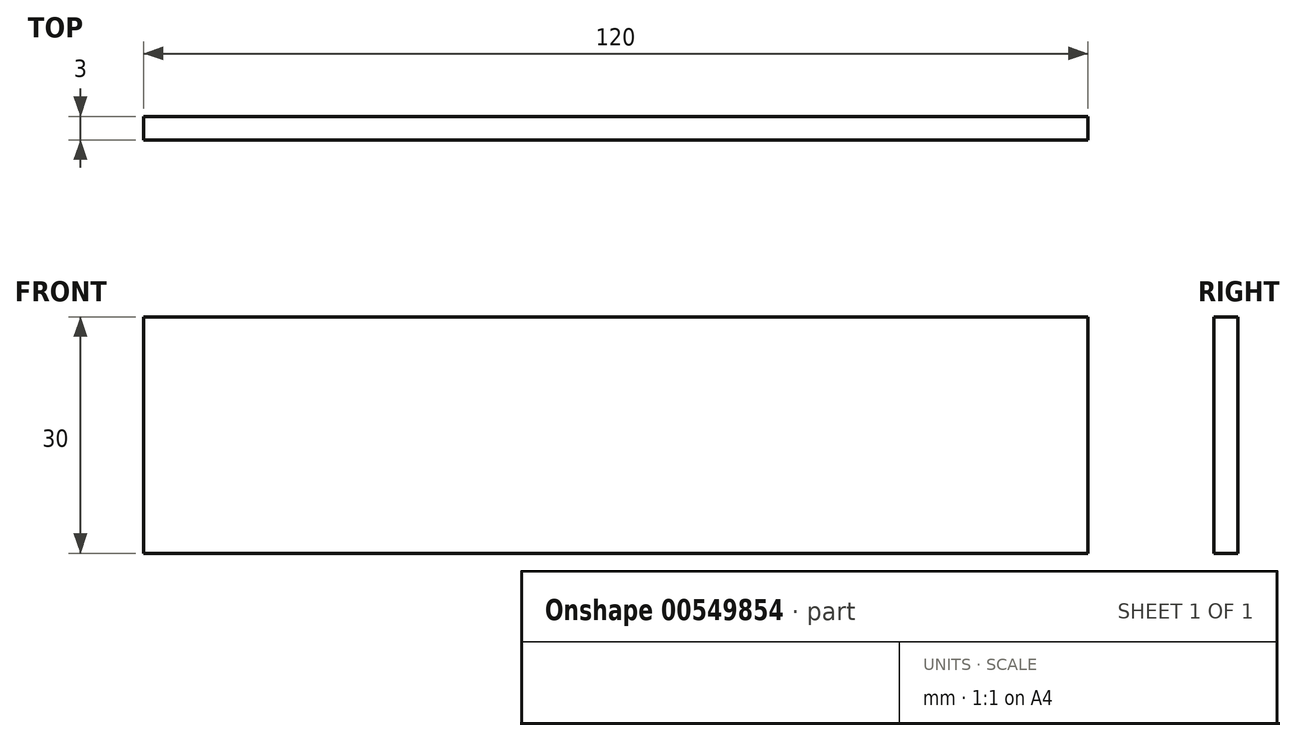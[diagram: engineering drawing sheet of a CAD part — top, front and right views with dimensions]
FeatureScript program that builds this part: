
annotation { "Feature Type Name" : "Feature", "Feature Type Description" : "" }
export const myFeature = defineFeature(function(context is Context, id is Id, definition is map)
    precondition{}
    {
        {
            var Q0;
            Q0=qCreatedBy(makeId("Front.planeOp"),FACE);
            var sketch = newSketch(context, id + "F0", { "sketchPlane" : qUnion([Q0])});
            skLineSegment(sketch, "E0.bottom", {"start": v(0, 0) * mm, "end": v(120, 0) * mm});
            skLineSegment(sketch, "E0.top", {"start": v(0, 30) * mm, "end": v(120, 30) * mm});
            skLineSegment(sketch, "E0.left", {"start": v(0, 0) * mm, "end": v(0, 30) * mm});
            skLineSegment(sketch, "E0.right", {"start": v(120, 0) * mm, "end": v(120, 30) * mm});
            skSolve(sketch);
        }
        {
            var Q0;
            Q0=makeQuery(id+"F0.imprint","IMPRINT",FACE,{"disambiguationData":[TD([[makeQuery(id+"F0.imprint","IMPRINT",EDGE,{"derivedFrom":sQuery(id+"F0.wireOp",EDGE,"E0.bottom")}),1.0]])]});
            extrude(context, id + "F1", {"entities" : qUnion([Q0]), "depth" : 3 * mm, "offsetDistance" : 25 * mm});
        }
    });
